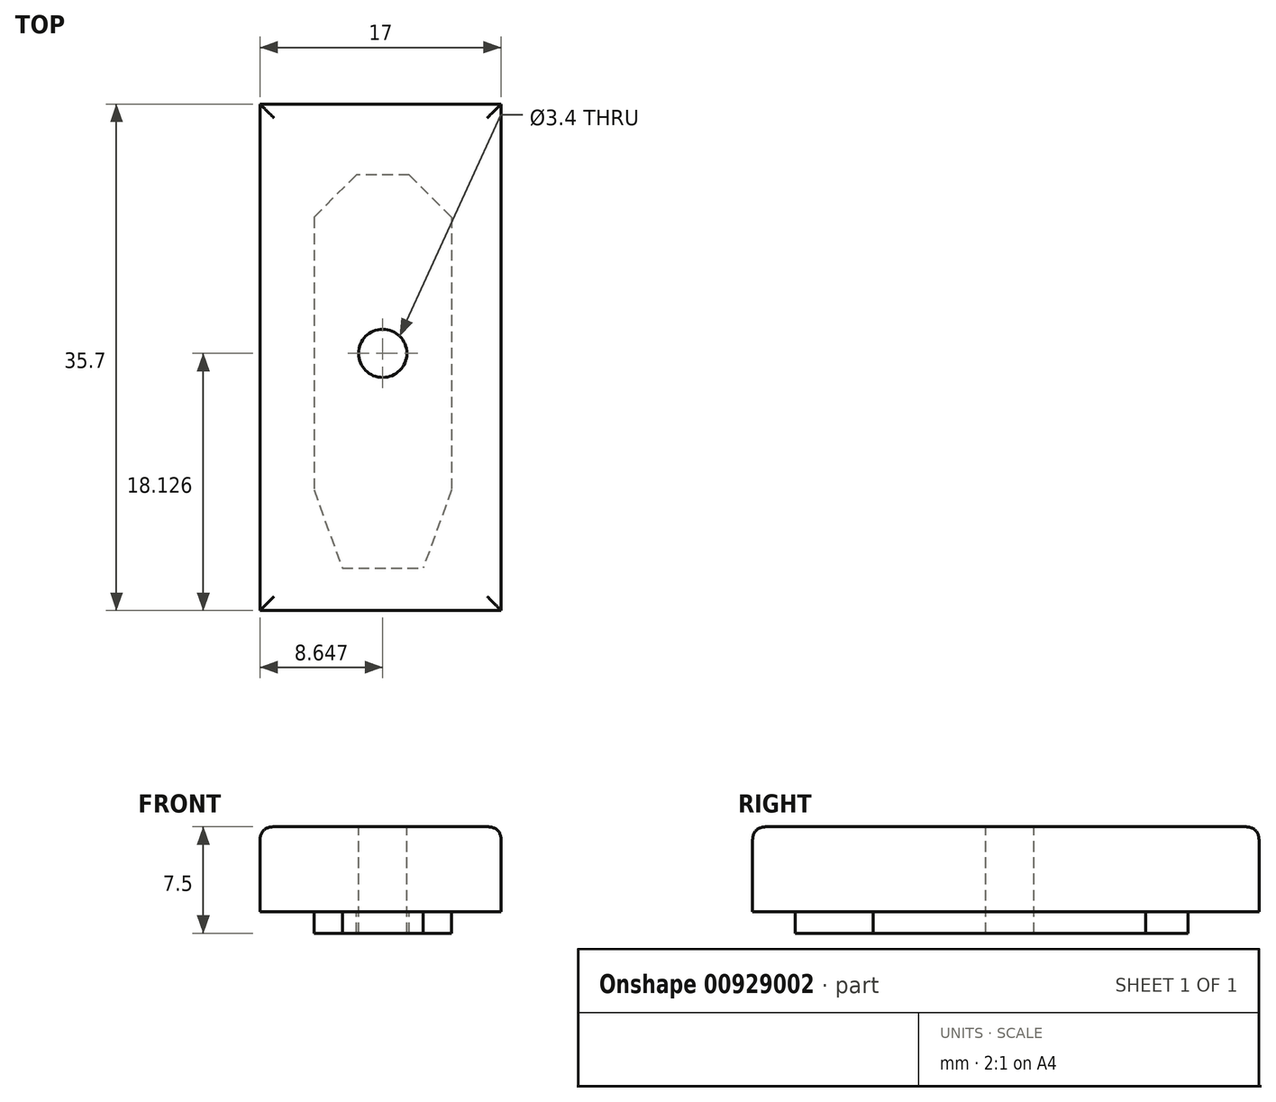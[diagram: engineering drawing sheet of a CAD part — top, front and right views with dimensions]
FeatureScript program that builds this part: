
annotation { "Feature Type Name" : "Feature", "Feature Type Description" : "" }
export const myFeature = defineFeature(function(context is Context, id is Id, definition is map)
    precondition{}
    {
        {
            var Q0;
            Q0=qCreatedBy(makeId("Top.planeOp"),FACE);
            var sketch = newSketch(context, id + "F0", { "sketchPlane" : qUnion([Q0])});
            skLineSegment(sketch, "E0", {"start": v(-25.55, 0.44) * mm, "end": v(37.22, 0.44) * mm, "construction": true});
            skLineSegment(sketch, "E1", {"start": v(0.13, -28.92) * mm, "end": v(0.13, 34.5) * mm, "construction": true});
            skLineSegment(sketch, "E2.1", {"start": v(-4.72, -9.2) * mm, "end": v(-2.72, -14.69) * mm});
            skLineSegment(sketch, "E2.2", {"start": v(0.13, 13.01) * mm, "end": v(-1.74, 13.01) * mm});
            skLineSegment(sketch, "E2.3", {"start": v(-1.74, 13.01) * mm, "end": v(-4.72, 10.03) * mm});
            skLineSegment(sketch, "E2.4", {"start": v(-4.72, 10.03) * mm, "end": v(-4.72, 0.44) * mm});
            skLineSegment(sketch, "E2.5", {"start": v(-4.72, 0.44) * mm, "end": v(-4.72, -9.2) * mm});
            skLineSegment(sketch, "E3.MirrorCS", {"start": v(0.13, 13.01) * mm, "end": v(2, 13.01) * mm});
            skLineSegment(sketch, "E4.MirrorCS", {"start": v(2, 13.01) * mm, "end": v(4.98, 10.03) * mm});
            skLineSegment(sketch, "E5.MirrorCS", {"start": v(4.98, 10.03) * mm, "end": v(4.98, 0.44) * mm});
            skLineSegment(sketch, "E6.MirrorCS", {"start": v(4.98, 0.44) * mm, "end": v(4.98, -9.2) * mm});
            skLineSegment(sketch, "E7.MirrorCS", {"start": v(4.98, -9.2) * mm, "end": v(2.98, -14.69) * mm});
            skCircle(sketch, "E8", {"center": v(0.13, 0.44) * mm, "radius": 1.7 * mm});
            skLineSegment(sketch, "E9", {"start": v(-2.72, -14.69) * mm, "end": v(2.98, -14.69) * mm});
            skLineSegment(sketch, "E10", {"start": v(0.13, -17.69) * mm, "end": v(-8.52, -17.69) * mm});
            skLineSegment(sketch, "E11", {"start": v(0.13, -17.69) * mm, "end": v(4.98, -17.69) * mm});
            skLineSegment(sketch, "E12", {"start": v(4.98, -17.69) * mm, "end": v(8.48, -17.69) * mm});
            skLineSegment(sketch, "E13", {"start": v(8.48, -17.69) * mm, "end": v(8.48, 18.01) * mm});
            skLineSegment(sketch, "E14", {"start": v(8.48, 18.01) * mm, "end": v(-8.52, 18.01) * mm});
            skLineSegment(sketch, "E15", {"start": v(-8.52, 18.01) * mm, "end": v(-8.52, -17.69) * mm});
            skSolve(sketch);
        }
        {
            var Q0;
            Q0=makeQuery(id+"F0.imprint","IMPRINT",FACE,{"disambiguationData":[TD([[makeQuery(id+"F0.imprint","IMPRINT",EDGE,{"derivedFrom":sQuery(id+"F0.wireOp",EDGE,"E2.1")}),1.0]])]});
            extrude(context, id + "F1", {"entities" : qUnion([Q0]), "oppositeDirection" : true, "depth" : 1.5 * mm, "offsetDistance" : 25 * mm, "hasSecondDirection" : true, "secondDirectionOppositeDirection" : false, "secondDirectionDepth" : 6 * mm});
        }
        {
            var Q0;
            Q0=makeQuery(id+"F0.imprint","IMPRINT",FACE,{"disambiguationData":[TD([[makeQuery(id+"F0.imprint","IMPRINT",EDGE,{"derivedFrom":sQuery(id+"F0.wireOp",EDGE,"E2.1")}),-1.0]])]});
            extrude(context, id + "F2", {"entities" : qUnion([Q0]), "operationType" : NewBodyOperationType.ADD, "depth" : 6 * mm, "offsetDistance" : 25 * mm});
        }
        {
            var Q0;
            Q0=makeQuery(id+"F2.opExtrude","CAP_EDGE",EDGE,{"disambiguationData":[OSD([sQuery(id+"F0.wireOp",EDGE,"E14")])],"isStart":false});
            var Q1;
            Q1=makeQuery(id+"F2.opExtrude","CAP_EDGE",EDGE,{"disambiguationData":[OSD([sQuery(id+"F0.wireOp",EDGE,"E15")])],"isStart":false});
            var Q2;
            Q2=makeQuery(id+"F2.opExtrude","CAP_EDGE",EDGE,{"disambiguationData":[OSD([sQuery(id+"F0.wireOp",EDGE,"E13")])],"isStart":false});
            var Q3;
            Q3=makeQuery(id+"F2.opExtrude","CAP_EDGE",EDGE,{"disambiguationData":[OSD([sQuery(id+"F0.wireOp",EDGE,"E10"),sQuery(id+"F0.wireOp",EDGE,"E11"),sQuery(id+"F0.wireOp",EDGE,"E12")])],"isStart":false});
            fillet(context, id + "F3", {"entities" : qUnion([Q0, Q1, Q2, Q3]), "radius" : 1 * mm, "tangentPropagation" : true, "rho" : 0.5, "crossSection" : FilletCrossSection.CONIC, "allowEdgeOverflow" : false});
        }
    });
